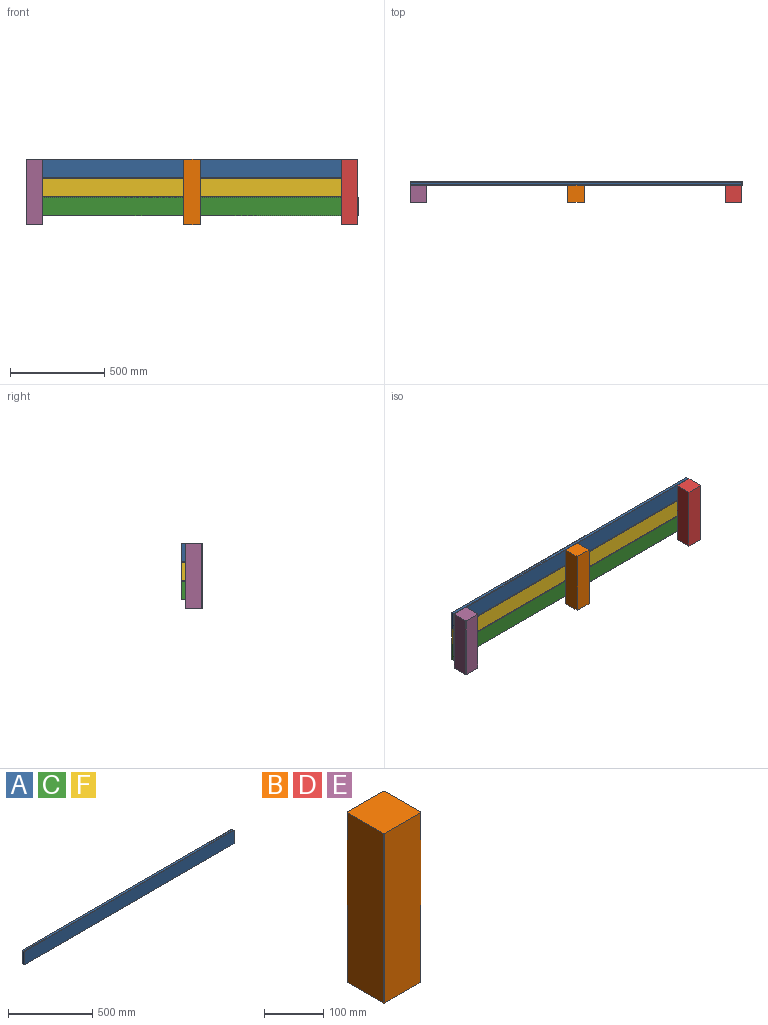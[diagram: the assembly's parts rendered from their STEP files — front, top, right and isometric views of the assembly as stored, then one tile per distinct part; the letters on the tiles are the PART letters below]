
ASSEMBLY  parts=6 mates=5
PART A: 10 faces, bbox 1764x18x100 mm
  f0: plane 1764x96mm, normal (0,1,0), area 169344mm2, adj f1,f3,f6,f8
  f1: plane 100x18mm, normal (-1,0,0), area 1792mm2, adj f0,f2,f4,f5,f6,f7,f8,f9
  f2: plane 1764x96mm, normal (0,-1,0), area 169344mm2, adj f1,f3,f7,f9
  f3: plane 100x18mm, normal (1,0,0), area 1792mm2, adj f0,f2,f4,f5,f6,f7,f8,f9
  f4: plane 1764x14mm, normal (0,0,1), area 24696mm2, adj f1,f3,f8,f9
  f5: plane 1764x14mm, normal (0,0,-1), area 24696mm2, adj f1,f3,f6,f7
  f6: plane 1764x2mm, normal (0,0.71,-0.71), area 4989.3mm2, adj f0,f1,f3,f5
  f7: plane 1764x2mm, normal (0,-0.71,-0.71), area 4989.3mm2, adj f1,f2,f3,f5
  f8: plane 1764x2mm, normal (0,0.71,0.71), area 4989.3mm2, adj f0,f1,f3,f4
  f9: plane 1764x2mm, normal (0,-0.71,0.71), area 4989.3mm2, adj f1,f2,f3,f4
PART B: 10 faces, bbox 90x90x350 mm
  f0: plane 350x86mm, normal (0,-1,0), area 30100mm2, adj f4,f5,f6,f7
  f1: plane 350x86mm, normal (1,0,0), area 30100mm2, adj f4,f5,f6,f9
  f2: plane 350x86mm, normal (0,1,0), area 30100mm2, adj f4,f5,f8,f9
  f3: plane 350x86mm, normal (-1,0,0), area 30100mm2, adj f4,f5,f7,f8
  f4: plane 90x90mm, normal (0,0,1), area 8092mm2, adj f0,f1,f2,f3,f6,f7,f8,f9
  f5: plane 90x90mm, normal (0,0,-1), area 8092mm2, adj f0,f1,f2,f3,f6,f7,f8,f9
  f6: plane 350x2mm, normal (0.71,-0.71,0), area 989.9mm2, adj f0,f1,f4,f5
  f7: plane 350x2mm, normal (-0.71,-0.71,0), area 989.9mm2, adj f0,f3,f4,f5
  f8: plane 350x2mm, normal (-0.71,0.71,0), area 989.9mm2, adj f2,f3,f4,f5
  f9: plane 350x2mm, normal (0.71,0.71,0), area 989.9mm2, adj f1,f2,f4,f5
PART C: same geometry as A
PART D: same geometry as B
PART E: same geometry as B
PART F: same geometry as A
PLACE A rot(axis=(0,0,-1),180deg) t=(81.57,-850.09,351.16)mm
PLACE B rot(axis=(0,0,-1),180deg) t=(107.35,-663.99,101.16)mm
PLACE C rot(axis=(0,0,-1),180deg) t=(81.57,-850.09,149.16)mm
PLACE D rot(axis=(0,0,1),180deg) t=(944.35,-663.99,101.16)mm
PLACE E rot(axis=(0,0,1),90deg) t=(-699.23,-739.25,101.16)mm
PLACE F rot(axis=(0,0,-1),180deg) t=(81.57,-850.09,250.16)mm
MATE fastened B.f0 <-> A.f0  axis (0,1,0) through (84.93,-671.83,451.16)mm
MATE fastened F.f0 <-> B.f0  axis (0,-1,0) through (84.93,-671.83,300.16)mm
MATE fastened B.f0 <-> C.f0  axis (0,1,0) through (84.93,-671.83,276.16)mm
MATE fastened D.f0 <-> A.f0  axis (0,1,0) through (964.93,-671.83,451.16)mm
MATE fastened A.f0 <-> E.f1  axis (0,-1,0) through (-797.07,-671.83,449.16)mm
